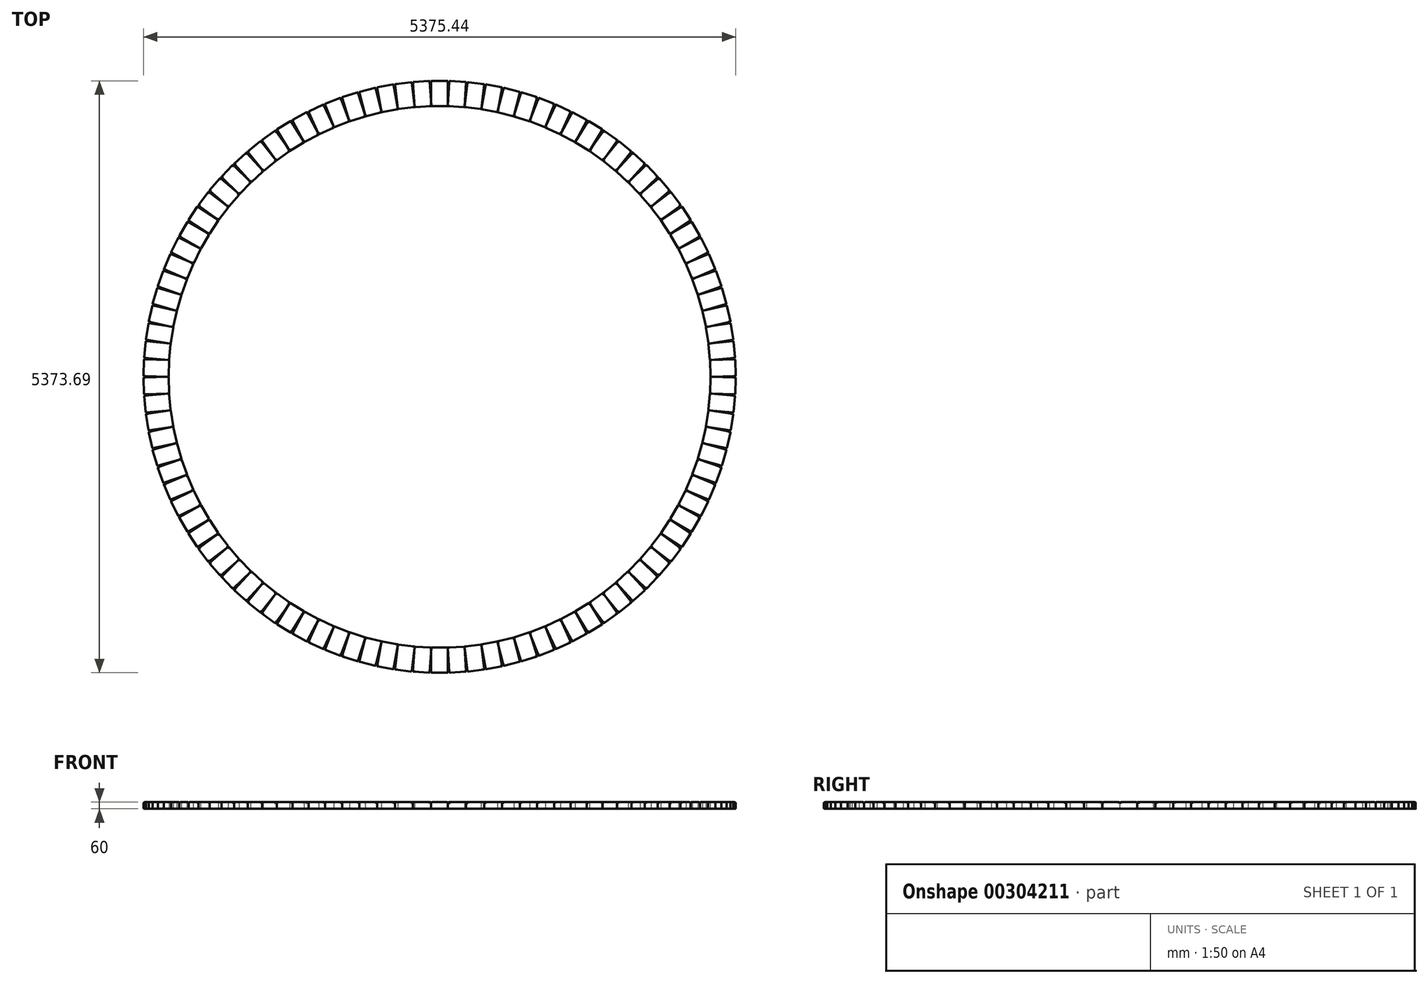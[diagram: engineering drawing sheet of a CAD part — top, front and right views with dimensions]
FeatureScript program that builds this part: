
annotation { "Feature Type Name" : "Feature", "Feature Type Description" : "" }
export const myFeature = defineFeature(function(context is Context, id is Id, definition is map)
    precondition{}
    {
        {
            var Q0;
            Q0=qCreatedBy(makeId("Top.planeOp"),FACE);
            var sketch = newSketch(context, id + "F0", { "sketchPlane" : qUnion([Q0])});
            skLineSegment(sketch, "E0", {"start": v(-2019.3, 0) * mm, "end": v(2019.3, 0) * mm, "construction": true});
            skPoint(sketch, "E1", {"position": v(0, 0) * mm});
            skCircle(sketch, "E2", {"center": v(0, -1772.44) * mm, "radius": 2686.84 * mm, "construction": true});
            skLineSegment(sketch, "E3", {"start": v(0, -1772.44) * mm, "end": v(0, 914.4) * mm, "construction": true});
            skLineSegment(sketch, "E4.bottom", {"start": v(-69.85, 914.4) * mm, "end": v(69.85, 914.4) * mm});
            skLineSegment(sketch, "E4.top", {"start": v(-69.85, 685.8) * mm, "end": v(69.85, 685.8) * mm});
            skLineSegment(sketch, "E4.left", {"start": v(-76.2, 908.05) * mm, "end": v(-76.2, 692.15) * mm});
            skLineSegment(sketch, "E4.right", {"start": v(76.2, 908.05) * mm, "end": v(76.2, 692.15) * mm});
            skPoint(sketch, "E5", {"position": v(0, 914.4) * mm});
            skPoint(sketch, "E6.visualSharp", {"position": v(-76.2, 914.4) * mm});
            skArc(sketch, "E6.filletArc", {"start": v(-69.85, 914.4) * mm, "mid": v(-74.34, 912.54) * mm, "end": v(-76.2, 908.05) * mm});
            skPoint(sketch, "E7.visualSharp", {"position": v(76.2, 914.4) * mm});
            skArc(sketch, "E7.filletArc", {"start": v(76.2, 908.05) * mm, "mid": v(74.34, 912.54) * mm, "end": v(69.85, 914.4) * mm});
            skPoint(sketch, "E8.visualSharp", {"position": v(76.2, 685.8) * mm});
            skArc(sketch, "E8.filletArc", {"start": v(69.85, 685.8) * mm, "mid": v(74.34, 687.66) * mm, "end": v(76.2, 692.15) * mm});
            skPoint(sketch, "E9.visualSharp", {"position": v(-76.2, 685.8) * mm});
            skArc(sketch, "E9.filletArc", {"start": v(-76.2, 692.15) * mm, "mid": v(-74.34, 687.66) * mm, "end": v(-69.85, 685.8) * mm});
            skSolve(sketch);
        }
        {
            var Q0;
            Q0 = qSketchRegion(id + "F0", true);
            extrude(context, id + "F1", {"entities" : qUnion([Q0]), "depth" : 60 * mm});
        }
        {
            var Q0;
            Q0=makeQuery(id+"F1.opExtrude","CAP_EDGE",EDGE,{"disambiguationData":[OSD([sQuery(id+"F0.wireOp",EDGE,"E4.left")])],"isStart":false});
            fillet(context, id + "F2", {"entities" : qUnion([Q0]), "radius" : 9.52 * mm, "tangentPropagation" : true, "allowEdgeOverflow" : false});
        }
        {
            var Q0;
            Q0=qCreatedBy(makeId("Right.planeOp"),FACE);
            var sketch = newSketch(context, id + "F3", { "sketchPlane" : qUnion([Q0])});
            skLineSegment(sketch, "E10", {"start": v(-1772.44, 0) * mm, "end": v(-1772.44, 304.8) * mm, "construction": true});
            skSolve(sketch);
        }
        {
            var Q0;
            Q0=makeQuery(id+"F1.opExtrude","SWEPT_BODY",BODY,{"disambiguationData":[OSD([sQuery(id+"F0.wireOp",EDGE,"E4.bottom"),sQuery(id+"F0.wireOp",EDGE,"E4.top"),sQuery(id+"F0.wireOp",EDGE,"E4.left"),sQuery(id+"F0.wireOp",EDGE,"E4.right"),sQuery(id+"F0.wireOp",EDGE,"E6.filletArc"),sQuery(id+"F0.wireOp",EDGE,"E7.filletArc"),sQuery(id+"F0.wireOp",EDGE,"E8.filletArc"),sQuery(id+"F0.wireOp",EDGE,"E9.filletArc")])]});
            var Q1;
            Q1=sQuery(id+"F3.wireOp",EDGE,"E10");
            circularPattern(context, id + "F4", {"entities" : qUnion([Q0]), "axis" : qUnion([Q1]), "angle" : 360 * degree, "instanceCount" : 102, "equalSpace" : true});
        }
    });
